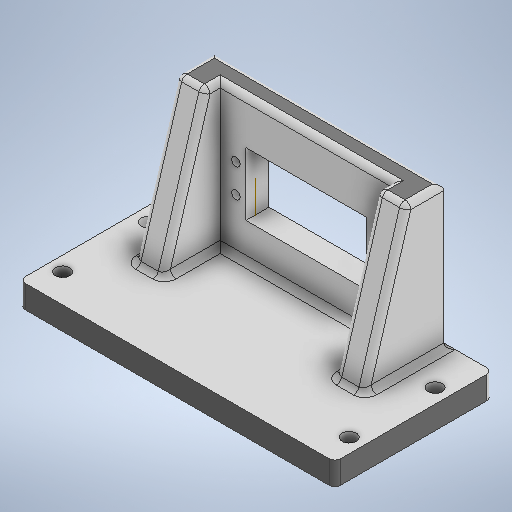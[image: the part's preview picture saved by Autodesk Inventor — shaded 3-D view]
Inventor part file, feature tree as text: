
AUTODESK INVENTOR PART (.ipt)
format: ipt  version: 2025.2 (Build 292293000, 293)  size: 471,552 bytes
history: native  units: mm
features: sketch x21, extrude x15, fillet x4, other x2, mirror x2, hole x1
ambient origin geometry x8: Origin, YZ Plane, XZ Plane, XY Plane, X Axis, Y Axis, Z Axis, Center Point
bodies: Body1 (feature_tree)
feature tree (45):
  other  "Bryła1"
  extrude  "Wyciągnięcie proste1"  Depth=110.0mm
  fillet  "Zaokrąglenie1"  Radius=90.0mm
  extrude  "Wyciągnięcie proste2"  Depth=8.0mm TaperAngle=0.0deg
  sketch  "Szkic8"
  sketch  "Szkic10"
  extrude  "Wyciągnięcie proste4"  Depth=2.0mm
  extrude  "Wyciągnięcie proste5"  Depth=22.0mm
  fillet  "Zaokrąglenie2"  Radius=22.0mm
  sketch  "Szkic15"
  sketch  "Szkic18"
  hole  "Otwór4"  [1 undecoded]
  extrude  "Wyciągnięcie proste10"  Depth=20.0mm
  mirror  "Odbij1"
  extrude  "Wyciągnięcie proste11"  Depth=10.0mm
  fillet  "Zaokrąglenie4"  Radius=20.0mm
  extrude  "Wyciągnięcie proste12"  Depth=64.0mm
  other  "Płaszczyzna konstrukcyjna1"
  extrude  "Wyciągnięcie proste13"  Depth=8.0mm
  extrude  "Wyciągnięcie proste14"  Depth=50.0mm TaperAngle=0.0deg
  sketch  "Szkic27"
  extrude  "Wyciągnięcie proste15"  Depth=20.0mm TaperAngle=0.0deg
  extrude  "Wyciągnięcie proste16"  Depth=25.0mm TaperAngle=0.0deg
  extrude  "Wyciągnięcie proste17"  Depth=2.0mm
  extrude  "Wyciągnięcie proste18"  Depth=5.0mm
  extrude  "Wyciągnięcie proste19"  Depth=5.0mm
  extrude  "Wyciągnięcie proste20"  Depth=5.0mm
  mirror  "Odbij5"
  fillet  "Zaokrąglenie6"  Radius=40.0mm
  sketch  "Szkic1"
  sketch  "Szkic5"
  sketch  "Szkic13"
  sketch  "Szkic14"
  sketch  "Szkic20"
  sketch  "Szkic22"
  sketch  "Szkic23"
  sketch  "Szkic24"
  sketch  "Szkic25"
  sketch  "Szkic26"
  sketch  "Szkic28"
  sketch  "Szkic29"
  sketch  "Szkic30"
  sketch  "Szkic31"
  sketch  "Szkic32"
  sketch  "Szkic33"
note: 1 required parameter value undecoded (feature->parameter linkage not recoverable at this tier; creation-order binding heuristic only, values carry confidence <= 0.55)
